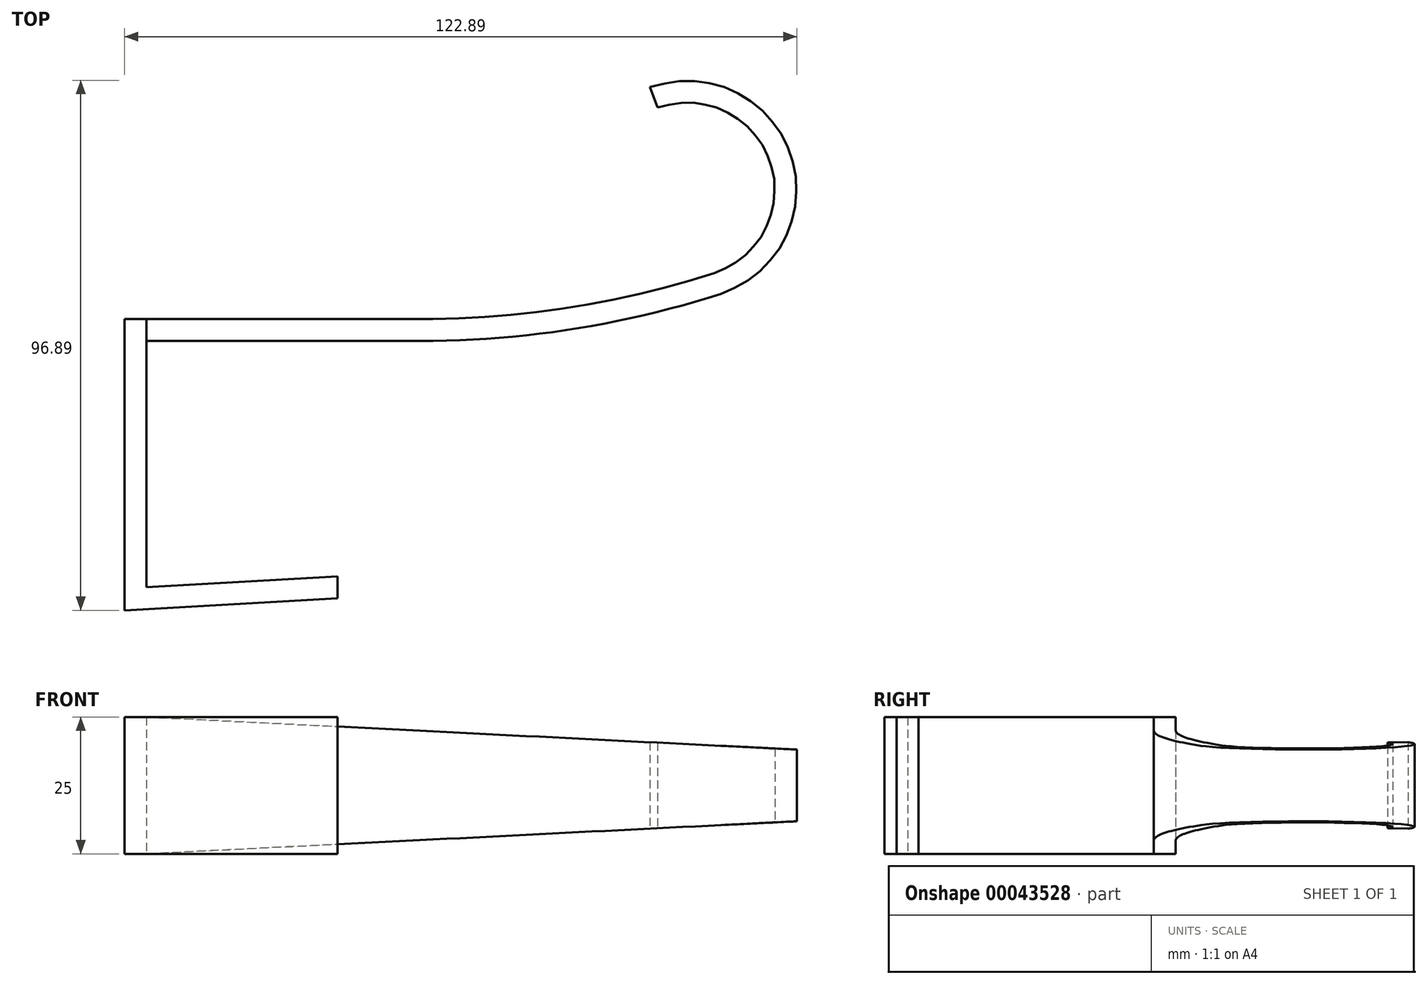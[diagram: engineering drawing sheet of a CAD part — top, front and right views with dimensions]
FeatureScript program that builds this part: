
annotation { "Feature Type Name" : "Feature", "Feature Type Description" : "" }
export const myFeature = defineFeature(function(context is Context, id is Id, definition is map)
    precondition{}
    {
        {
            var Q0;
            Q0=qCreatedBy(makeId("Top.planeOp"),FACE);
            var sketch = newSketch(context, id + "F0", { "sketchPlane" : qUnion([Q0])});
            skLineSegment(sketch, "E0", {"start": v(0, 0) * mm, "end": v(-34.94, -2) * mm});
            skLineSegment(sketch, "E1", {"start": v(-34.94, -2) * mm, "end": v(-34.94, 43) * mm});
            skLineSegment(sketch, "E2", {"start": v(-34.94, 43) * mm, "end": v(15.06, 43) * mm});
            skArc(sketch, "E3", {"start": v(15.06, 43) * mm, "mid": v(42.9, 45.17) * mm, "end": v(70.06, 51.6) * mm});
            skArc(sketch, "E4", {"start": v(70.06, 51.6) * mm, "mid": v(82.87, 77.13) * mm, "end": v(57.1, 89.45) * mm});
            skArc(sketch, "E5.0", {"start": v(68.83, 55.42) * mm, "mid": v(79.08, 75.83) * mm, "end": v(58.47, 85.69) * mm});
            skLineSegment(sketch, "E5.1", {"start": v(0, -4) * mm, "end": v(-38.94, -6.24) * mm});
            skLineSegment(sketch, "E5.2", {"start": v(-38.94, -6.24) * mm, "end": v(-38.94, 47) * mm});
            skLineSegment(sketch, "E5.3", {"start": v(-38.94, 47) * mm, "end": v(15.06, 47) * mm});
            skArc(sketch, "E5.4", {"start": v(15.06, 47) * mm, "mid": v(42.27, 49.12) * mm, "end": v(68.83, 55.42) * mm});
            skLineSegment(sketch, "E6", {"start": v(58.47, 85.69) * mm, "end": v(57.1, 89.45) * mm});
            skLineSegment(sketch, "E7", {"start": v(0, 0) * mm, "end": v(0, -4) * mm});
            skLineSegment(sketch, "E8", {"start": v(63.95, 70.65) * mm, "end": v(58.47, 85.69) * mm, "construction": true});
            skLineSegment(sketch, "E9", {"start": v(63.95, 70.65) * mm, "end": v(63.95, 83.25) * mm, "construction": true});
            skSolve(sketch);
        }
        {
            var Q0;
            Q0=makeQuery(id+"F0.imprint","IMPRINT",FACE,{"disambiguationData":[TD([[makeQuery(id+"F0.imprint","IMPRINT",EDGE,{"derivedFrom":sQuery(id+"F0.wireOp",EDGE,"E0")}),1.0]])]});
            extrude(context, id + "F1", {"entities" : qUnion([Q0]), "depth" : 25 * mm});
        }
        {
            var Q0;
            Q0=makeQuery(id+"F1.opExtrude","SWEPT_FACE",FACE,{"disambiguationData":[OSD([sQuery(id+"F0.wireOp",EDGE,"E2")])]});
            var sketch = newSketch(context, id + "F2", { "sketchPlane" : qUnion([Q0])});
            skLineSegment(sketch, "E10", {"start": v(-34.94, 25) * mm, "end": v(85.06, 19) * mm});
            skLineSegment(sketch, "E11", {"start": v(-34.94, 0) * mm, "end": v(85.06, 6) * mm});
            skLineSegment(sketch, "E12.0", {"start": v(-34.94, 25) * mm, "end": v(-34.94, 0) * mm});
            skLineSegment(sketch, "E13", {"start": v(-34.94, 12.5) * mm, "end": v(85.06, 12.5) * mm, "construction": true});
            skLineSegment(sketch, "E14", {"start": v(85.06, 19) * mm, "end": v(85.06, 6) * mm});
            skLineSegment(sketch, "E15", {"start": v(-34.94, 25) * mm, "end": v(85.06, 25) * mm});
            skLineSegment(sketch, "E16", {"start": v(85.06, 19) * mm, "end": v(85.06, 25) * mm});
            skLineSegment(sketch, "E17", {"start": v(-34.94, 0) * mm, "end": v(85.06, 0) * mm});
            skLineSegment(sketch, "E18", {"start": v(85.06, 0) * mm, "end": v(85.06, 6) * mm});
            skSolve(sketch);
        }
        {
            var Q0;
            {var subQ5=sQuery(id+"F2.wireOp",EDGE,"E16");Q0=makeQuery(id+"F2.imprint","IMPRINT",FACE,{"disambiguationData":[TD([[makeQuery(id+"F2.imprint","IMPRINT",EDGE,{"derivedFrom":subQ5}),1.0]])]});}
            var Q1;
            {var subQ1=sQuery(id+"F2.wireOp",EDGE,"E10");var subQ3=sQuery(id+"F2.wireOp",EDGE,"E15");var subQ5=makeQuery(id+"F2.imprint","INTERSECT",VERTEX,{"derivedFrom":[subQ1,sQuery(id+"F2.wireOp",EDGE,"E12.0"),subQ3]});Q1=makeQuery(id+"F2.imprint","IMPRINT",FACE,{"disambiguationData":[TD([[makeQuery(id+"F2.imprint","IMPRINT",EDGE,{"disambiguationData":[TD([[subQ5,-1.0]])],"derivedFrom":subQ1}),1.0]])]});}
            var Q2;
            {var subQ1=sQuery(id+"F2.wireOp",EDGE,"E11");var subQ3=sQuery(id+"F2.wireOp",EDGE,"E17");var subQ5=makeQuery(id+"F2.imprint","INTERSECT",VERTEX,{"derivedFrom":[subQ1,sQuery(id+"F2.wireOp",EDGE,"E12.0"),subQ3]});Q2=makeQuery(id+"F2.imprint","IMPRINT",FACE,{"disambiguationData":[TD([[makeQuery(id+"F2.imprint","IMPRINT",EDGE,{"disambiguationData":[TD([[subQ5,-1.0]])],"derivedFrom":subQ1}),-1.0]])]});}
            var Q3;
            {var subQ5=sQuery(id+"F2.wireOp",EDGE,"E18");Q3=makeQuery(id+"F2.imprint","IMPRINT",FACE,{"disambiguationData":[TD([[makeQuery(id+"F2.imprint","IMPRINT",EDGE,{"derivedFrom":subQ5}),1.0]])]});}
            extrude(context, id + "F3", {"entities" : qUnion([Q0, Q1, Q2, Q3]), "operationType" : NewBodyOperationType.REMOVE, "endBound" : BoundingType.THROUGH_ALL, "oppositeDirection" : true, "depth" : 25 * mm});
        }
    });
